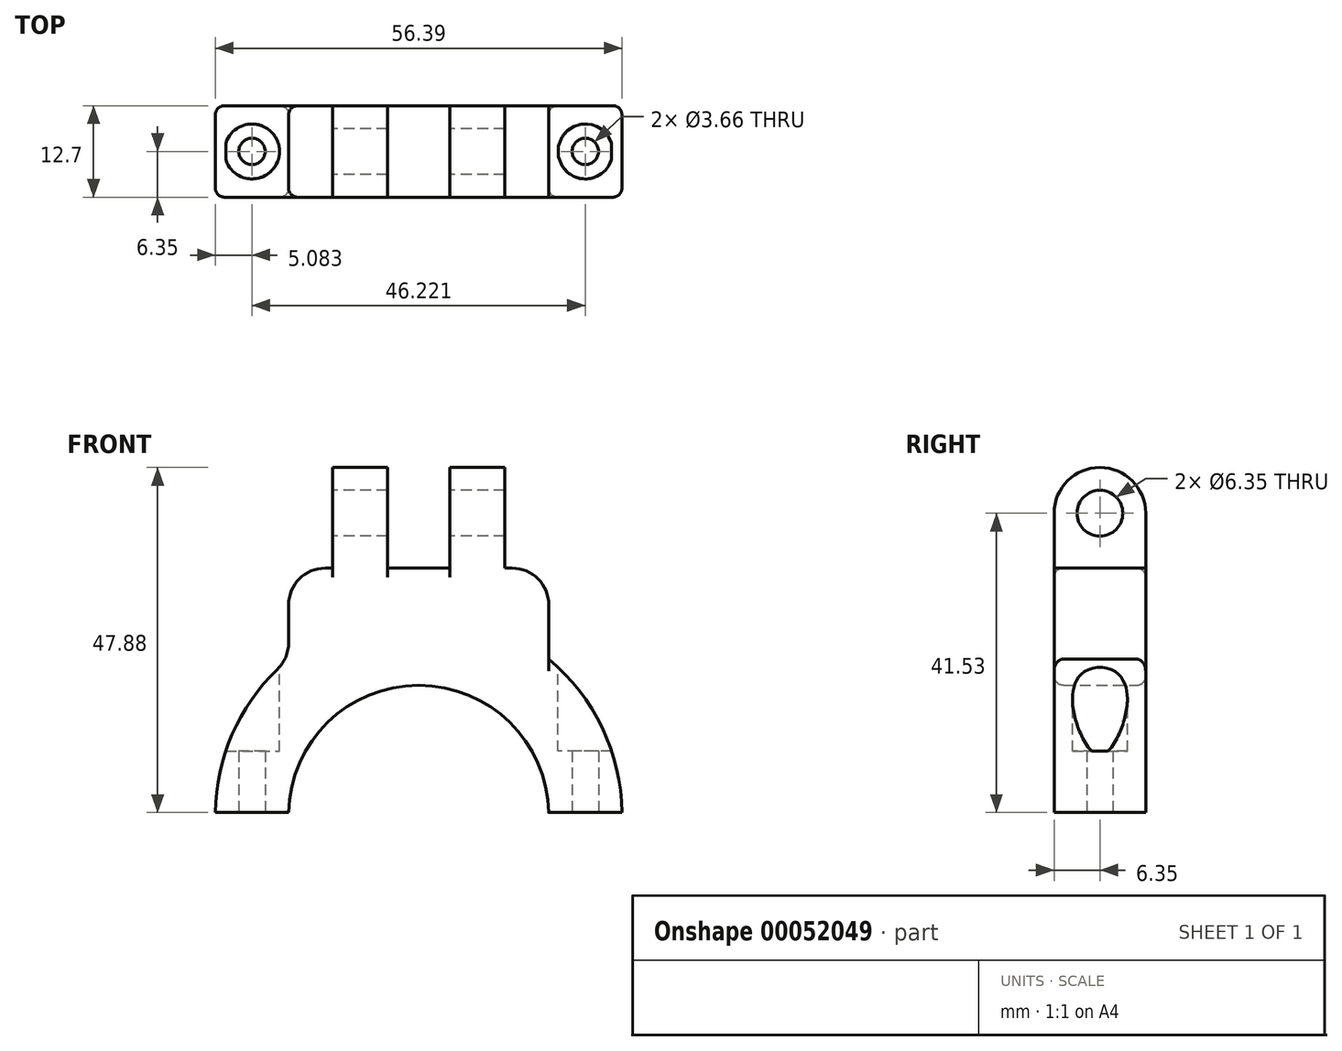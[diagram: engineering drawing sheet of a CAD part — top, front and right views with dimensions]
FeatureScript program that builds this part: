
annotation { "Feature Type Name" : "Feature", "Feature Type Description" : "" }
export const myFeature = defineFeature(function(context is Context, id is Id, definition is map)
    precondition{}
    {
        {
            var Q0;
            Q0=qCreatedBy(makeId("Front.planeOp"),FACE);
            var sketch = newSketch(context, id + "F0", { "sketchPlane" : qUnion([Q0])});
            skLineSegment(sketch, "E0", {"start": v(0, 0) * mm, "end": v(36.07, 0) * mm});
            skArc(sketch, "E1", {"start": v(36.07, 0) * mm, "mid": v(18.03, 18.03) * mm, "end": v(0, 0) * mm});
            skLineSegment(sketch, "E2", {"start": v(0, 0) * mm, "end": v(-10.16, 0) * mm});
            skLineSegment(sketch, "E3", {"start": v(36.07, 0) * mm, "end": v(46.23, 0) * mm});
            skArc(sketch, "E4", {"start": v(46.23, 0) * mm, "mid": v(18.03, 28.2) * mm, "end": v(-10.16, 0) * mm});
            skLineSegment(sketch, "E5", {"start": v(-10.16, 0) * mm, "end": v(-10.16, 0.38) * mm});
            skLineSegment(sketch, "E6", {"start": v(-10.16, 0.38) * mm, "end": v(0, 0.38) * mm});
            skLineSegment(sketch, "E7", {"start": v(46.23, 0) * mm, "end": v(46.23, 0.38) * mm});
            skLineSegment(sketch, "E8", {"start": v(46.23, 0.38) * mm, "end": v(36.06, 0.38) * mm});
            skSolve(sketch);
        }
        {
            var Q0;
            {var subQ0=sQuery(id+"F0.wireOp",EDGE,"E6");var subQ1=sQuery(id+"F0.wireOp",EDGE,"E1");var subQ2=makeQuery(id+"F0.imprint","INTERSECT",VERTEX,{"derivedFrom":[subQ1,subQ0]});Q0=makeQuery(id+"F0.imprint","IMPRINT",FACE,{"disambiguationData":[TD([[makeQuery(id+"F0.imprint","IMPRINT",EDGE,{"disambiguationData":[TD([[subQ2,1.0]])],"derivedFrom":subQ1}),-1.0]])]});}
            extrude(context, id + "F1", {"entities" : qUnion([Q0]), "depth" : 12.7 * mm});
        }
        {
            var Q0;
            Q0=qCreatedBy(makeId("Top.planeOp"),FACE);
            cPlane(context, id + "F2", {"entities" : qUnion([Q0]), "cplaneType" : CPlaneType.OFFSET, "offset" : 34.3 * mm, "width" : 152.4 * mm, "height" : 152.4 * mm});
        }
        {
            var Q0;
            Q0=qCreatedBy(id+"F2.planeOp",FACE);
            var sketch = newSketch(context, id + "F3", { "sketchPlane" : qUnion([Q0])});
            skLineSegment(sketch, "E9", {"start": v(0, 0) * mm, "end": v(18.03, 0) * mm});
            skLineSegment(sketch, "E10", {"start": v(0, 0) * mm, "end": v(0, -12.7) * mm});
            skLineSegment(sketch, "E11", {"start": v(18.03, 0) * mm, "end": v(36.07, 0) * mm});
            skLineSegment(sketch, "E12", {"start": v(36.07, 0) * mm, "end": v(36.07, -12.7) * mm});
            skLineSegment(sketch, "E13", {"start": v(36.07, -12.7) * mm, "end": v(0, -12.7) * mm});
            skSolve(sketch);
        }
        {
            var Q0;
            Q0 = qSketchRegion(id + "F3", true);
            var Q1;
            Q1=makeQuery(id+"F1.opExtrude","SWEPT_FACE",FACE,{"disambiguationData":[OSD([sQuery(id+"F0.wireOp",EDGE,"E4")])]});
            extrude(context, id + "F4", {"entities" : qUnion([Q0]), "operationType" : NewBodyOperationType.ADD, "endBound" : BoundingType.UP_TO_SURFACE, "oppositeDirection" : true, "endBoundEntityFace" : qUnion([Q1]), "depth" : 25.4 * mm});
        }
        {
            var Q0;
            Q0=makeQuery(id+"F4.opExtrude","CAP_FACE",FACE,{"disambiguationData":[OSD([sQuery(id+"F3.wireOp",EDGE,"E9"),sQuery(id+"F3.wireOp",EDGE,"E10"),sQuery(id+"F3.wireOp",EDGE,"E11"),sQuery(id+"F3.wireOp",EDGE,"E12"),sQuery(id+"F3.wireOp",EDGE,"E13")])],"isStart":true});
            var sketch = newSketch(context, id + "F5", { "sketchPlane" : qUnion([Q0])});
            skLineSegment(sketch, "E14", {"start": v(18.03, 0) * mm, "end": v(13.72, 0) * mm});
            skLineSegment(sketch, "E15", {"start": v(18.03, 0) * mm, "end": v(22.35, 0) * mm});
            skLineSegment(sketch, "E16", {"start": v(13.72, 0) * mm, "end": v(6.1, 0) * mm});
            skLineSegment(sketch, "E17", {"start": v(22.35, 0) * mm, "end": v(29.97, 0) * mm});
            skLineSegment(sketch, "E18", {"start": v(6.1, 0) * mm, "end": v(6.1, -12.7) * mm});
            skLineSegment(sketch, "E19", {"start": v(6.1, -12.7) * mm, "end": v(13.72, -12.7) * mm});
            skLineSegment(sketch, "E20", {"start": v(13.72, -12.7) * mm, "end": v(13.72, 0) * mm});
            skLineSegment(sketch, "E21", {"start": v(22.35, 0) * mm, "end": v(22.35, -12.7) * mm});
            skLineSegment(sketch, "E22", {"start": v(29.97, 0) * mm, "end": v(29.97, -12.7) * mm});
            skLineSegment(sketch, "E23", {"start": v(22.35, -12.7) * mm, "end": v(29.97, -12.7) * mm});
            skSolve(sketch);
        }
        {
            var Q0;
            Q0=makeQuery(id+"F5.imprint","IMPRINT",FACE,{"disambiguationData":[TD([[makeQuery(id+"F5.imprint","IMPRINT",EDGE,{"derivedFrom":sQuery(id+"F5.wireOp",EDGE,"E16")}),-1.0]])]});
            var Q1;
            Q1=makeQuery(id+"F5.imprint","IMPRINT",FACE,{"disambiguationData":[TD([[makeQuery(id+"F5.imprint","IMPRINT",EDGE,{"derivedFrom":sQuery(id+"F5.wireOp",EDGE,"E17")}),-1.0]])]});
            extrude(context, id + "F6", {"entities" : qUnion([Q0, Q1]), "operationType" : NewBodyOperationType.ADD, "depth" : 13.97 * mm});
        }
        {
            var Q0;
            Q0=makeQuery(id+"F6.opExtrude","SWEPT_FACE",FACE,{"disambiguationData":[OSD([sQuery(id+"F5.wireOp",EDGE,"E18")])]});
            var sketch = newSketch(context, id + "F7", { "sketchPlane" : qUnion([Q0])});
            skLineSegment(sketch, "E24", {"start": v(6.35, 48.26) * mm, "end": v(6.35, 41.91) * mm});
            skPoint(sketch, "E24.endSnap0", {"position": v(6.35, 48.26) * mm});
            skCircle(sketch, "E25", {"center": v(6.35, 41.91) * mm, "radius": 3.18 * mm});
            skSolve(sketch);
        }
        {
            var Q0;
            Q0 = qSketchRegion(id + "F7", true);
            var Q1;
            Q1=makeQuery(id+"F6.opExtrude","SWEPT_FACE",FACE,{"disambiguationData":[OSD([sQuery(id+"F5.wireOp",EDGE,"E22")])]});
            extrude(context, id + "F8", {"entities" : qUnion([Q0]), "operationType" : NewBodyOperationType.REMOVE, "endBound" : BoundingType.UP_TO_SURFACE, "oppositeDirection" : true, "endBoundEntityFace" : qUnion([Q1]), "depth" : 25.4 * mm});
        }
        {
            var Q0;
            Q0=makeQuery(id+"F6.opExtrude","CAP_EDGE",EDGE,{"disambiguationData":[OSD([sQuery(id+"F5.wireOp",EDGE,"E19")])],"isStart":false});
            var Q1;
            Q1=makeQuery(id+"F6.opExtrude","CAP_EDGE",EDGE,{"disambiguationData":[OSD([sQuery(id+"F5.wireOp",EDGE,"E23")])],"isStart":false});
            var Q2;
            Q2=makeQuery(id+"F6.opExtrude","CAP_EDGE",EDGE,{"disambiguationData":[OSD([sQuery(id+"F5.wireOp",EDGE,"E16")])],"isStart":false});
            var Q3;
            Q3=makeQuery(id+"F6.opExtrude","CAP_EDGE",EDGE,{"disambiguationData":[OSD([sQuery(id+"F5.wireOp",EDGE,"E17")])],"isStart":false});
            fillet(context, id + "F9", {"entities" : qUnion([Q0, Q1, Q2, Q3]), "radius" : 6.35 * mm, "tangentPropagation" : true, "allowEdgeOverflow" : false});
        }
        {
            var Q0;
            Q0=makeQuery(id+"F4.opExtrude","CAP_EDGE",EDGE,{"disambiguationData":[OSD([sQuery(id+"F3.wireOp",EDGE,"E12")])],"isStart":true});
            var Q1;
            Q1=makeQuery(id+"F4.opExtrude","CAP_EDGE",EDGE,{"disambiguationData":[OSD([sQuery(id+"F3.wireOp",EDGE,"E12")])],"isStart":false});
            var Q2;
            Q2=makeQuery(id+"F4.opExtrude","CAP_EDGE",EDGE,{"disambiguationData":[OSD([sQuery(id+"F3.wireOp",EDGE,"E10")])],"isStart":true});
            var Q3;
            Q3=makeQuery(id+"F4.opExtrude","CAP_EDGE",EDGE,{"disambiguationData":[OSD([sQuery(id+"F3.wireOp",EDGE,"E10")])],"isStart":false});
            fillet(context, id + "F10", {"entities" : qUnion([Q0, Q1, Q2, Q3]), "radius" : 5.08 * mm, "tangentPropagation" : true, "allowEdgeOverflow" : false});
        }
        {
            var Q0;
            Q0=makeQuery(id+"F1.opExtrude","SWEPT_FACE",FACE,{"disambiguationData":[OSD([sQuery(id+"F0.wireOp",EDGE,"E6")])]});
            var sketch = newSketch(context, id + "F11", { "sketchPlane" : qUnion([Q0])});
            skLineSegment(sketch, "E26", {"start": v(-5.08, 0) * mm, "end": v(-5.08, 6.35) * mm});
            skCircle(sketch, "E27", {"center": v(-5.08, 6.35) * mm, "radius": 1.83 * mm});
            skSolve(sketch);
        }
        {
            var Q0;
            Q0=makeQuery(id+"F11.imprint","IMPRINT",FACE,{"disambiguationData":[TD([[makeQuery(id+"F11.imprint","IMPRINT",EDGE,{"derivedFrom":sQuery(id+"F11.wireOp",EDGE,"E27")}),1.0]])]});
            var Q1;
            {var subQ0=sQuery(id+"F0.wireOp",EDGE,"E6");var subQ2=sQuery(id+"F0.wireOp",EDGE,"E4");Q1=makeQuery(id+"F4.boolean.opBoolean","SPLIT",FACE,{"disambiguationData":[TD([makeQuery(id+"F1.opExtrude","SWEPT_FACE",FACE,{"disambiguationData":[OSD([subQ0])]})])],"derivedFrom":makeQuery(id+"F1.opExtrude","SWEPT_FACE",FACE,{"disambiguationData":[OSD([subQ2])]})});}
            extrude(context, id + "F12", {"entities" : qUnion([Q0]), "operationType" : NewBodyOperationType.REMOVE, "endBound" : BoundingType.UP_TO_SURFACE, "oppositeDirection" : true, "endBoundEntityFace" : qUnion([Q1]), "depth" : 25.4 * mm});
        }
        {
            var Q0;
            Q0=makeQuery(id+"F1.opExtrude","SWEPT_FACE",FACE,{"disambiguationData":[OSD([sQuery(id+"F0.wireOp",EDGE,"E8")])]});
            var sketch = newSketch(context, id + "F13", { "sketchPlane" : qUnion([Q0])});
            skLineSegment(sketch, "E28", {"start": v(41.14, 0) * mm, "end": v(41.14, 6.35) * mm});
            skCircle(sketch, "E29", {"center": v(41.14, 6.35) * mm, "radius": 1.83 * mm});
            skSolve(sketch);
        }
        {
            var Q0;
            Q0=makeQuery(id+"F13.imprint","IMPRINT",FACE,{"disambiguationData":[TD([[makeQuery(id+"F13.imprint","IMPRINT",EDGE,{"derivedFrom":sQuery(id+"F13.wireOp",EDGE,"E29")}),1.0]])]});
            var Q1;
            {var subQ0=sQuery(id+"F0.wireOp",EDGE,"E8");var subQ2=sQuery(id+"F0.wireOp",EDGE,"E4");Q1=makeQuery(id+"F4.boolean.opBoolean","SPLIT",FACE,{"disambiguationData":[TD([makeQuery(id+"F1.opExtrude","SWEPT_FACE",FACE,{"disambiguationData":[OSD([subQ0])]})])],"derivedFrom":makeQuery(id+"F1.opExtrude","SWEPT_FACE",FACE,{"disambiguationData":[OSD([subQ2])]})});}
            extrude(context, id + "F14", {"entities" : qUnion([Q0]), "operationType" : NewBodyOperationType.REMOVE, "endBound" : BoundingType.UP_TO_SURFACE, "oppositeDirection" : true, "endBoundEntityFace" : qUnion([Q1]), "depth" : 25.4 * mm});
        }
        {
            var Q0;
            {var subQ0=sQuery(id+"F3.wireOp",EDGE,"E13");var subQ5=sQuery(id+"F3.wireOp",EDGE,"E11");var subQ6=sQuery(id+"F3.wireOp",EDGE,"E9");Q0=makeQuery(id+"F6.boolean.opBoolean","SPLIT",FACE,{"disambiguationData":[TD([makeQuery(id+"F6.opExtrude","SWEPT_FACE",FACE,{"disambiguationData":[OSD([sQuery(id+"F5.wireOp",EDGE,"E20")])]})])],"derivedFrom":makeQuery(id+"F4.opExtrude","CAP_FACE",FACE,{"disambiguationData":[OSD([subQ6,sQuery(id+"F3.wireOp",EDGE,"E10"),subQ5,sQuery(id+"F3.wireOp",EDGE,"E12"),subQ0])],"isStart":true})});}
            var sketch = newSketch(context, id + "F15", { "sketchPlane" : qUnion([Q0])});
            skLineSegment(sketch, "E30", {"start": v(-3.25, -6.35) * mm, "end": v(-5.08, -6.35) * mm});
            skLineSegment(sketch, "E31", {"start": v(41.14, -6.35) * mm, "end": v(39.32, -6.35) * mm});
            skCircle(sketch, "E32", {"center": v(-5.08, -6.35) * mm, "radius": 3.81 * mm});
            skCircle(sketch, "E33", {"center": v(41.14, -6.35) * mm, "radius": 3.81 * mm});
            skSolve(sketch);
        }
        {
            var Q0;
            Q0 = qSketchRegion(id + "F15", true);
            extrude(context, id + "F16", {"entities" : qUnion([Q0]), "operationType" : NewBodyOperationType.REMOVE, "oppositeDirection" : true, "depth" : 25.4 * mm});
        }
        {
            var Q0;
            Q0=makeQuery(id+"F1.opExtrude","CAP_EDGE",EDGE,{"disambiguationData":[OSD([sQuery(id+"F0.wireOp",EDGE,"E1")])],"isStart":true});
            var Q1;
            {var subQ0=sQuery(id+"F0.wireOp",EDGE,"E6");var subQ1=sQuery(id+"F0.wireOp",EDGE,"E4");Q1=makeQuery(id+"F4.boolean.opBoolean","SPLIT",EDGE,{"disambiguationData":[TD([makeQuery(id+"F1.opExtrude","SWEPT_FACE",FACE,{"disambiguationData":[OSD([subQ0])]})])],"derivedFrom":makeQuery(id+"F1.opExtrude","CAP_EDGE",EDGE,{"disambiguationData":[OSD([subQ1])],"isStart":true})});}
            var Q2;
            {var subQ0=sQuery(id+"F0.wireOp",EDGE,"E6");var subQ1=sQuery(id+"F0.wireOp",EDGE,"E4");Q2=makeQuery(id+"F4.boolean.opBoolean","SPLIT",EDGE,{"disambiguationData":[TD([makeQuery(id+"F1.opExtrude","SWEPT_FACE",FACE,{"disambiguationData":[OSD([subQ0])]})])],"derivedFrom":makeQuery(id+"F1.opExtrude","CAP_EDGE",EDGE,{"disambiguationData":[OSD([subQ1])],"isStart":false})});}
            var Q3;
            {var subQ0=sQuery(id+"F0.wireOp",EDGE,"E8");var subQ1=sQuery(id+"F0.wireOp",EDGE,"E4");Q3=makeQuery(id+"F4.boolean.opBoolean","SPLIT",EDGE,{"disambiguationData":[TD([makeQuery(id+"F1.opExtrude","SWEPT_FACE",FACE,{"disambiguationData":[OSD([subQ0])]})])],"derivedFrom":makeQuery(id+"F1.opExtrude","CAP_EDGE",EDGE,{"disambiguationData":[OSD([subQ1])],"isStart":false})});}
            var Q4;
            Q4=makeQuery(id+"F1.opExtrude","CAP_EDGE",EDGE,{"disambiguationData":[OSD([sQuery(id+"F0.wireOp",EDGE,"E1")])],"isStart":false});
            var Q5;
            {var subQ0=sQuery(id+"F0.wireOp",EDGE,"E8");var subQ1=sQuery(id+"F0.wireOp",EDGE,"E4");Q5=makeQuery(id+"F4.boolean.opBoolean","SPLIT",EDGE,{"disambiguationData":[TD([makeQuery(id+"F1.opExtrude","SWEPT_FACE",FACE,{"disambiguationData":[OSD([subQ0])]})])],"derivedFrom":makeQuery(id+"F1.opExtrude","CAP_EDGE",EDGE,{"disambiguationData":[OSD([subQ1])],"isStart":true})});}
            var Q6;
            {var subQ0=sQuery(id+"F3.wireOp",EDGE,"E13");Q6=makeQuery(id+"F6.boolean.opBoolean","SPLIT",EDGE,{"disambiguationData":[TD([makeQuery(id+"F6.opExtrude","SWEPT_FACE",FACE,{"disambiguationData":[OSD([sQuery(id+"F5.wireOp",EDGE,"E20")])]})])],"derivedFrom":makeQuery(id+"F4.opExtrude","CAP_EDGE",EDGE,{"disambiguationData":[OSD([subQ0])],"isStart":true})});}
            var Q7;
            {var subQ0=sQuery(id+"F3.wireOp",EDGE,"E11");var subQ1=sQuery(id+"F3.wireOp",EDGE,"E9");Q7=makeQuery(id+"F6.boolean.opBoolean","SPLIT",EDGE,{"disambiguationData":[TD([makeQuery(id+"F6.opExtrude","SWEPT_FACE",FACE,{"disambiguationData":[OSD([sQuery(id+"F5.wireOp",EDGE,"E20")])]})])],"derivedFrom":makeQuery(id+"F4.opExtrude","CAP_EDGE",EDGE,{"disambiguationData":[OSD([subQ1,subQ0])],"isStart":true})});}
            fillet(context, id + "F17", {"entities" : qUnion([Q0, Q1, Q2, Q3, Q4, Q5, Q6, Q7]), "radius" : 1.27 * mm, "tangentPropagation" : true, "allowEdgeOverflow" : false});
        }
    });
